# Revit family: Door-French-Pella-Architect_Series-Sliding_Patio_Door-Fixed
name_source: partatom
category: Doors
revit_build: Autodesk Revit Architecture 2013 (Build: 20130531_2115(x64)
units: mm (PartAtom-declared; Revit-internal decimal feet)

## types (12) — shared parameters
Analytic Construction = <None>
Architectural Design Manual = www.pellaadm.com
Construction Type = -
Cross Grille Pattern = No
Custom Grille Pattern = No
Custom Horizontal Lites = 2
Custom Vertical Lites = 6
Description = Sliding French - Fixed Unit
Door Grille Visibility = Yes
Door Handle Height = 3' - 0"
Energy Efficiency = http://www.pella.com
Environmental Commitment = http://www.pella.com
Ext Finish = Aluminum - Pella - Brown
Function = Interior
Glazing Finish = Glass - Pella - Clear Insulating Glass
Glazing Thickness = 107/128"
Int Finish = Wood - Pella - Pine
Manufacturer = Pella - Windows & Doors
Note* = Maximum Frame Depth is 211 mm; if Wall Depth exceeds this value please recalculated Set Back to reflect
Operation = Sliding Patio Door
Prairie Grille Pattern = No
Product Documentation Link = http://media.pella.com
Product Name = Architect Series Sliding Patio Door
Product Page URL = http://www.pella.com
Series = Architect Series - Aluminum-Clad Wood
Top Row Grille Pattern = No
Traditional Grille Pattern = Yes
URL = www.pella.com
Wall Closure = By host

## per-type parameters (varying)
| type | C Height | C Width | DLO Height | DLO Width | Height | Hinges | Rough Height | Rough Width | Unit Height | Unit Width | Width |
| 3180 | 6' - 7 1/2" | 2' - 6 3/4" | 5' - 4 107/128" | 1' - 7 39/128" | 6' - 7 1/2" | 3 | 6' - 8" | 2' - 7 1/2" | 6' - 5 15/32" | 2' - 4 19/64" | 2' - 6 3/4" |
| 3181 | 6' - 8 1/8" | 2' - 6 3/4" | 5' - 5 59/128" | 1' - 7 39/128" | 6' - 8 1/8" | 3 | 6' - 8 5/8" | 2' - 7 1/2" | 6' - 6 3/32" | 2' - 4 19/64" | 2' - 6 3/4" |
| 3182 | 6' - 9 1/2" | 2' - 6 3/4" | 5' - 6 107/128" | 1' - 7 39/128" | 6' - 9 1/2" | 3 | 6' - 10" | 2' - 7 1/2" | 6' - 7 15/32" | 2' - 4 19/64" | 2' - 6 3/4" |
| 3196 | 7' - 11 1/2" | 2' - 6 3/4" | 6' - 8 107/128" | 1' - 7 39/128" | 7' - 11 1/2" | 4 | 8' - 0" | 2' - 7 1/2" | 7' - 9 15/32" | 2' - 4 19/64" | 2' - 6 3/4" |
| 3780 | 6' - 7 1/2" | 3' - 0 3/4" | 5' - 4 107/128" | 2' - 1 39/128" | 6' - 7 1/2" | 3 | 6' - 8" | 3' - 1 1/2" | 6' - 5 15/32" | 2' - 10 19/64" | 3' - 0 3/4" |
| 3781 | 6' - 8 1/8" | 3' - 0 3/4" | 5' - 5 59/128" | 2' - 1 39/128" | 6' - 8 1/8" | 3 | 6' - 8 5/8" | 3' - 1 1/2" | 6' - 6 3/32" | 2' - 10 19/64" | 3' - 0 3/4" |
| 3782 | 6' - 9 1/2" | 3' - 0 3/4" | 5' - 6 107/128" | 2' - 1 39/128" | 6' - 9 1/2" | 3 | 6' - 10" | 3' - 1 1/2" | 6' - 7 15/32" | 2' - 10 19/64" | 3' - 0 3/4" |
| 3796 | 7' - 11 1/2" | 3' - 0 3/4" | 6' - 8 107/128" | 2' - 1 39/128" | 7' - 11 1/2" | 4 | 8' - 0" | 3' - 1 1/2" | 7' - 9 15/32" | 2' - 10 19/64" | 3' - 0 3/4" |
| 4980 | 6' - 7 1/2" | 4' - 0 3/4" | 5' - 4 107/128" | 3' - 1 39/128" | 6' - 7 1/2" | 3 | 6' - 8" | 4' - 1 1/2" | 6' - 5 15/32" | 3' - 10 19/64" | 4' - 0 3/4" |
| 4981 | 6' - 8 1/8" | 4' - 0 3/4" | 5' - 5 59/128" | 3' - 1 39/128" | 6' - 8 1/8" | 3 | 6' - 8 5/8" | 4' - 1 1/2" | 6' - 6 3/32" | 3' - 10 19/64" | 4' - 0 3/4" |
| 4962 | 6' - 9 1/2" | 4' - 0 3/4" | 5' - 6 107/128" | 3' - 1 39/128" | 6' - 9 1/2" | 3 | 6' - 10" | 4' - 1 1/2" | 6' - 7 15/32" | 3' - 10 19/64" | 4' - 0 3/4" |
| 4996 | 7' - 11 1/2" | 4' - 0 3/4" | 6' - 8 107/128" | 3' - 1 39/128" | 7' - 11 1/2" | 4 | 8' - 0" | 4' - 1 1/2" | 7' - 9 15/32" | 3' - 10 19/64" | 4' - 0 3/4" |

note: column(s) folded — value = type name in every type: Model

## geometry (parser evidence)
native form markers: Blend x4, Sweep x7
no freeform markers — native parametric forms only
